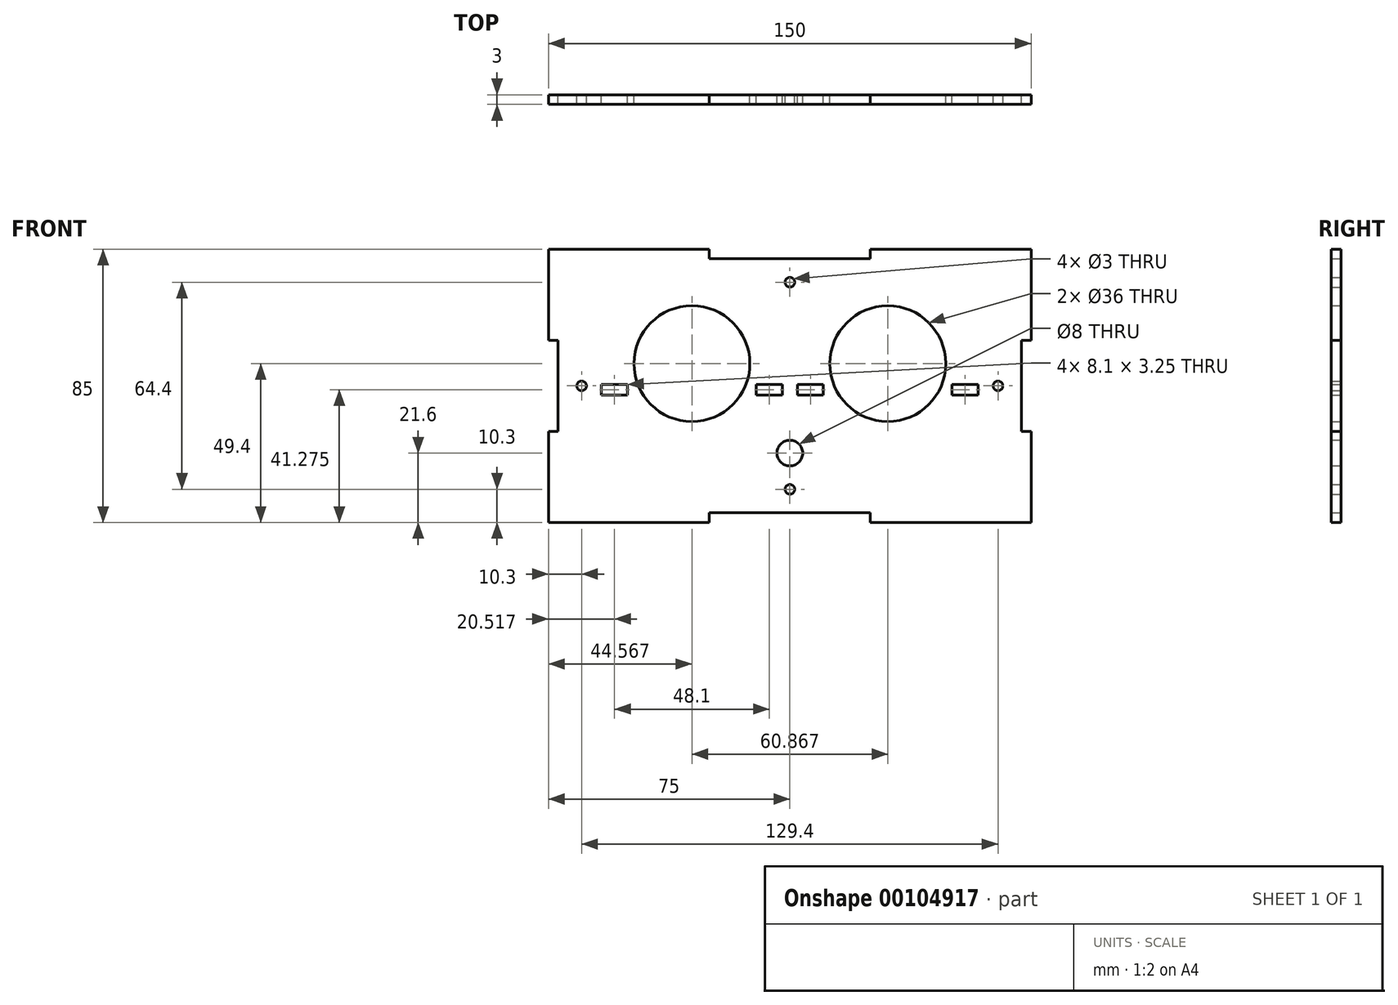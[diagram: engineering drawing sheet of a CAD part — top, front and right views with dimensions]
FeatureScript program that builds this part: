
annotation { "Feature Type Name" : "Feature", "Feature Type Description" : "" }
export const myFeature = defineFeature(function(context is Context, id is Id, definition is map)
    precondition{}
    {
        {
            var Q0;
            Q0=qCreatedBy(makeId("Front.planeOp"),FACE);
            var sketch = newSketch(context, id + "F0", { "sketchPlane" : qUnion([Q0])});
            skLineSegment(sketch, "E0.top", {"start": v(-75, -42.5) * mm, "end": v(-25, -42.5) * mm});
            skLineSegment(sketch, "E0.left", {"start": v(-75, 42.5) * mm, "end": v(-75, 14.17) * mm});
            skLineSegment(sketch, "E0.right", {"start": v(75, 42.5) * mm, "end": v(75, 14.17) * mm});
            skLineSegment(sketch, "E1", {"start": v(-75, 42.5) * mm, "end": v(-25, 42.5) * mm});
            skLineSegment(sketch, "E2", {"start": v(-25, 42.5) * mm, "end": v(-25, 39.5) * mm});
            skLineSegment(sketch, "E3", {"start": v(-25, 39.5) * mm, "end": v(25, 39.5) * mm});
            skLineSegment(sketch, "E4", {"start": v(25, 39.5) * mm, "end": v(25, 42.5) * mm});
            skLineSegment(sketch, "E5", {"start": v(25, 42.5) * mm, "end": v(75, 42.5) * mm});
            skLineSegment(sketch, "E6", {"start": v(75, 14.17) * mm, "end": v(72, 14.17) * mm});
            skLineSegment(sketch, "E7", {"start": v(72, 14.17) * mm, "end": v(72, -14.17) * mm});
            skLineSegment(sketch, "E8", {"start": v(72, -14.17) * mm, "end": v(75, -14.17) * mm});
            skLineSegment(sketch, "E9.trimOffspring", {"start": v(75, -14.17) * mm, "end": v(75, -42.5) * mm});
            skLineSegment(sketch, "E10", {"start": v(-75, 14.17) * mm, "end": v(-72, 14.17) * mm});
            skLineSegment(sketch, "E11", {"start": v(-72, 14.17) * mm, "end": v(-72, -14.17) * mm});
            skLineSegment(sketch, "E12", {"start": v(-72, -14.17) * mm, "end": v(-75, -14.17) * mm});
            skLineSegment(sketch, "E13", {"start": v(-25, -42.5) * mm, "end": v(-25, -39.5) * mm});
            skLineSegment(sketch, "E14", {"start": v(-25, -39.5) * mm, "end": v(25, -39.5) * mm});
            skLineSegment(sketch, "E15", {"start": v(25, -39.5) * mm, "end": v(25, -42.5) * mm});
            skLineSegment(sketch, "E16.trimOffspring", {"start": v(-75, -14.17) * mm, "end": v(-75, -42.5) * mm});
            skLineSegment(sketch, "E17.trimOffspring", {"start": v(25, -42.5) * mm, "end": v(75, -42.5) * mm});
            skCircle(sketch, "E18", {"center": v(0, -20.9) * mm, "radius": 4 * mm});
            skCircle(sketch, "E19", {"center": v(0, 32.2) * mm, "radius": 1.5 * mm});
            skCircle(sketch, "E20", {"center": v(64.7, 0) * mm, "radius": 1.5 * mm});
            skCircle(sketch, "E21", {"center": v(0, -32.2) * mm, "radius": 1.5 * mm});
            skCircle(sketch, "E22", {"center": v(-64.7, 0) * mm, "radius": 1.5 * mm});
            skCircle(sketch, "E23", {"center": v(-30.43, 6.9) * mm, "radius": 18 * mm});
            skLineSegment(sketch, "E24.bottom", {"start": v(-10.43, 0.4) * mm, "end": v(-2.33, 0.4) * mm});
            skLineSegment(sketch, "E24.top", {"start": v(-10.43, -2.85) * mm, "end": v(-2.33, -2.85) * mm});
            skLineSegment(sketch, "E24.left", {"start": v(-10.43, 0.4) * mm, "end": v(-10.43, -2.85) * mm});
            skLineSegment(sketch, "E24.right", {"start": v(-2.33, 0.4) * mm, "end": v(-2.33, -2.85) * mm});
            skLineSegment(sketch, "E25.bottom", {"start": v(-50.43, 0.4) * mm, "end": v(-58.53, 0.4) * mm});
            skLineSegment(sketch, "E25.top", {"start": v(-50.43, -2.85) * mm, "end": v(-58.53, -2.85) * mm});
            skLineSegment(sketch, "E25.left", {"start": v(-50.43, 0.4) * mm, "end": v(-50.43, -2.85) * mm});
            skLineSegment(sketch, "E25.right", {"start": v(-58.53, 0.4) * mm, "end": v(-58.53, -2.85) * mm});
            skLineSegment(sketch, "E26", {"start": v(-72, 0) * mm, "end": v(-64.7, 0) * mm, "construction": true});
            skLineSegment(sketch, "E27", {"start": v(64.7, 0) * mm, "end": v(72, 0) * mm, "construction": true});
            skLineSegment(sketch, "E28", {"start": v(-75, 24.9) * mm, "end": v(75, 24.9) * mm, "construction": true});
            skLineSegment(sketch, "E29", {"start": v(-75, -11.1) * mm, "end": v(75, -11.1) * mm, "construction": true});
            skLineSegment(sketch, "E30", {"start": v(0, 30.7) * mm, "end": v(0, 24.9) * mm, "construction": true});
            skLineSegment(sketch, "E31", {"start": v(0, -16.9) * mm, "end": v(0, -11.1) * mm, "construction": true});
            skLineSegment(sketch, "E32", {"start": v(0, -30.7) * mm, "end": v(0, -24.9) * mm, "construction": true});
            skLineSegment(sketch, "E33", {"start": v(0, 39.5) * mm, "end": v(0, -39.5) * mm, "construction": true});
            skLineSegment(sketch, "E34.MirrorCS", {"start": v(2.33, 0.4) * mm, "end": v(2.33, -2.85) * mm});
            skLineSegment(sketch, "E35.MirrorCS", {"start": v(10.43, 0.4) * mm, "end": v(10.43, -2.85) * mm});
            skLineSegment(sketch, "E36.MirrorCS", {"start": v(50.43, 0.4) * mm, "end": v(50.43, -2.85) * mm});
            skLineSegment(sketch, "E37.MirrorCS", {"start": v(58.53, 0.4) * mm, "end": v(58.53, -2.85) * mm});
            skLineSegment(sketch, "E38.MirrorCS", {"start": v(10.43, -2.85) * mm, "end": v(2.33, -2.85) * mm});
            skLineSegment(sketch, "E39.MirrorCS", {"start": v(50.43, 0.4) * mm, "end": v(58.53, 0.4) * mm});
            skCircle(sketch, "E40.MirrorC", {"center": v(30.43, 6.9) * mm, "radius": 18 * mm});
            skLineSegment(sketch, "E41.MirrorCS", {"start": v(10.43, 0.4) * mm, "end": v(2.33, 0.4) * mm});
            skLineSegment(sketch, "E42.MirrorCS", {"start": v(50.43, -2.85) * mm, "end": v(58.53, -2.85) * mm});
            skLineSegment(sketch, "E43", {"start": v(-58.53, 0) * mm, "end": v(-63.2, 0) * mm});
            skLineSegment(sketch, "E44", {"start": v(58.53, 0) * mm, "end": v(63.2, 0) * mm, "construction": true});
            skLineSegment(sketch, "E45", {"start": v(-2.33, -1.22) * mm, "end": v(2.33, -1.22) * mm, "construction": true});
            skSolve(sketch);
        }
        {
            var Q0;
            Q0=qSketchRegion(id+"F0",true);
            extrude(context, id + "F1", {"entities" : qUnion([Q0]), "depth" : 3 * mm});
        }
        {
            var Q0;
            Q0=makeQuery(id+"F1.opExtrude","SWEPT_BODY",BODY,{"disambiguationData":[OSD([sQuery(id+"F0.wireOp",EDGE,"E0.top"),sQuery(id+"F0.wireOp",EDGE,"E0.left"),sQuery(id+"F0.wireOp",EDGE,"E0.right"),sQuery(id+"F0.wireOp",EDGE,"E1"),sQuery(id+"F0.wireOp",EDGE,"E2"),sQuery(id+"F0.wireOp",EDGE,"E3"),sQuery(id+"F0.wireOp",EDGE,"E4"),sQuery(id+"F0.wireOp",EDGE,"E5"),sQuery(id+"F0.wireOp",EDGE,"E6"),sQuery(id+"F0.wireOp",EDGE,"E7"),sQuery(id+"F0.wireOp",EDGE,"E8"),sQuery(id+"F0.wireOp",EDGE,"E9.trimOffspring"),sQuery(id+"F0.wireOp",EDGE,"E10"),sQuery(id+"F0.wireOp",EDGE,"E11"),sQuery(id+"F0.wireOp",EDGE,"E12"),sQuery(id+"F0.wireOp",EDGE,"E13"),sQuery(id+"F0.wireOp",EDGE,"E14"),sQuery(id+"F0.wireOp",EDGE,"E15"),sQuery(id+"F0.wireOp",EDGE,"E16.trimOffspring"),sQuery(id+"F0.wireOp",EDGE,"E17.trimOffspring"),sQuery(id+"F0.wireOp",EDGE,"iJvMOkkT-Gsvz-D80s-Lrck-NuYzV2775GFc"),sQuery(id+"F0.wireOp",EDGE,"95r7G61u-81NE-ogXZ-HZlh-HaEjHri7Uc5C"),sQuery(id+"F0.wireOp",EDGE,"kNa5tEdO-uy4Q-kRTS-gWff-R1CwjTJMmlwP"),sQuery(id+"F0.wireOp",EDGE,"NSmLs8Xq-7i2g-OZIT-hmmc-yelxhuIJ4KvX"),sQuery(id+"F0.wireOp",EDGE,"4YweHJoU-akzP-T6YO-Ozvt-s9SiKn9Ip7Ij"),sQuery(id+"F0.wireOp",EDGE,"DRZYSCKz-exI7-oD3f-2VZ2-mNw9MquuhidN"),sQuery(id+"F0.wireOp",EDGE,"cFZweqHX-i8zY-QQJQ-dr00-DEtuZUepJHJH"),sQuery(id+"F0.wireOp",EDGE,"vflKgIvX-I86b-ziDt-TOTA-sqA9vDxPemz3"),sQuery(id+"F0.wireOp",EDGE,"E18"),sQuery(id+"F0.wireOp",EDGE,"E19"),sQuery(id+"F0.wireOp",EDGE,"E20"),sQuery(id+"F0.wireOp",EDGE,"E21"),sQuery(id+"F0.wireOp",EDGE,"E22")])]});
            transform(context, id + "F2", {"entities" : qUnion([Q0]), "transformType" : TransformType.TRANSLATION_3D, "dx" : 0 * mm, "dy" : 60 * mm, "dz" : 0 * mm, "makeCopy" : true});
        }
        {
            var Q0;
            Q0=makeQuery(id+"F2.opPattern","COPY",BODY,{"derivedFrom":makeQuery(id+"F1.opExtrude","SWEPT_BODY",BODY,{"disambiguationData":[OSD([sQuery(id+"F0.wireOp",EDGE,"E0.top"),sQuery(id+"F0.wireOp",EDGE,"E0.left"),sQuery(id+"F0.wireOp",EDGE,"E0.right"),sQuery(id+"F0.wireOp",EDGE,"E1"),sQuery(id+"F0.wireOp",EDGE,"E2"),sQuery(id+"F0.wireOp",EDGE,"E3"),sQuery(id+"F0.wireOp",EDGE,"E4"),sQuery(id+"F0.wireOp",EDGE,"E5"),sQuery(id+"F0.wireOp",EDGE,"E6"),sQuery(id+"F0.wireOp",EDGE,"E7"),sQuery(id+"F0.wireOp",EDGE,"E8"),sQuery(id+"F0.wireOp",EDGE,"E9.trimOffspring"),sQuery(id+"F0.wireOp",EDGE,"E10"),sQuery(id+"F0.wireOp",EDGE,"E11"),sQuery(id+"F0.wireOp",EDGE,"E12"),sQuery(id+"F0.wireOp",EDGE,"E13"),sQuery(id+"F0.wireOp",EDGE,"E14"),sQuery(id+"F0.wireOp",EDGE,"E15"),sQuery(id+"F0.wireOp",EDGE,"E16.trimOffspring"),sQuery(id+"F0.wireOp",EDGE,"E17.trimOffspring"),sQuery(id+"F0.wireOp",EDGE,"iJvMOkkT-Gsvz-D80s-Lrck-NuYzV2775GFc"),sQuery(id+"F0.wireOp",EDGE,"95r7G61u-81NE-ogXZ-HZlh-HaEjHri7Uc5C"),sQuery(id+"F0.wireOp",EDGE,"kNa5tEdO-uy4Q-kRTS-gWff-R1CwjTJMmlwP"),sQuery(id+"F0.wireOp",EDGE,"NSmLs8Xq-7i2g-OZIT-hmmc-yelxhuIJ4KvX"),sQuery(id+"F0.wireOp",EDGE,"4YweHJoU-akzP-T6YO-Ozvt-s9SiKn9Ip7Ij"),sQuery(id+"F0.wireOp",EDGE,"DRZYSCKz-exI7-oD3f-2VZ2-mNw9MquuhidN"),sQuery(id+"F0.wireOp",EDGE,"cFZweqHX-i8zY-QQJQ-dr00-DEtuZUepJHJH"),sQuery(id+"F0.wireOp",EDGE,"vflKgIvX-I86b-ziDt-TOTA-sqA9vDxPemz3"),sQuery(id+"F0.wireOp",EDGE,"E18"),sQuery(id+"F0.wireOp",EDGE,"E19"),sQuery(id+"F0.wireOp",EDGE,"E20"),sQuery(id+"F0.wireOp",EDGE,"E21"),sQuery(id+"F0.wireOp",EDGE,"E22")])]}),"instanceName":"1"});
            deleteBodies(context, id + "F3", {"entities" : qUnion([Q0])});
        }
    });
